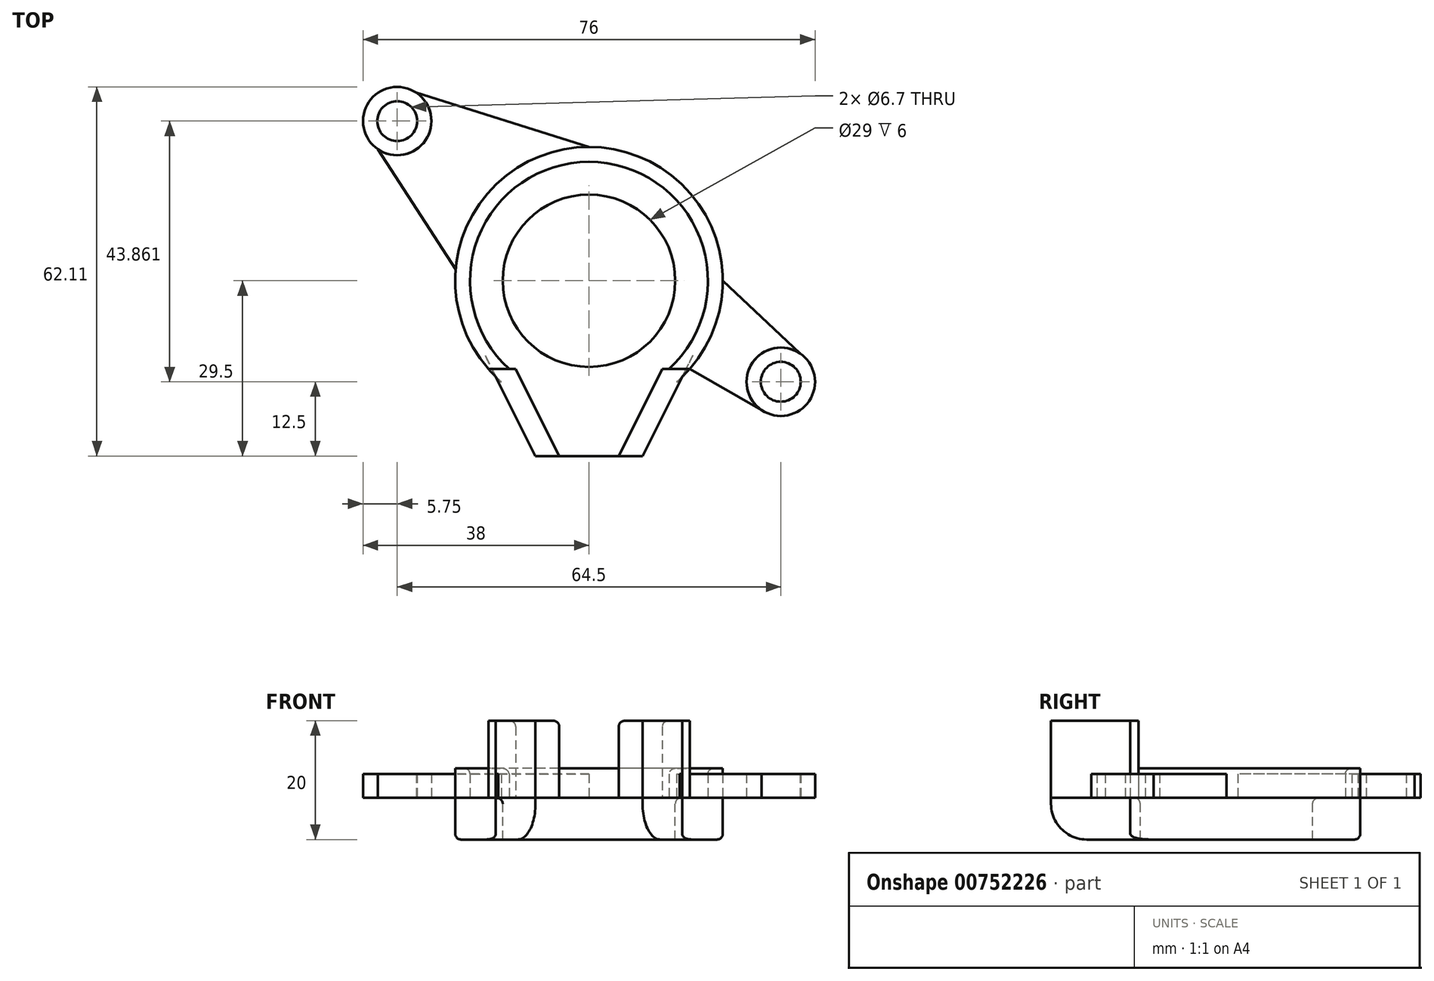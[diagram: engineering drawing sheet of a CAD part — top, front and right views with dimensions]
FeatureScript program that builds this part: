
annotation { "Feature Type Name" : "Feature", "Feature Type Description" : "" }
export const myFeature = defineFeature(function(context is Context, id is Id, definition is map)
    precondition{}
    {
        {
            var Q0;
            Q0=qCreatedBy(makeId("Top.planeOp"),FACE);
            var sketch = newSketch(context, id + "F0", { "sketchPlane" : qUnion([Q0])});
            skCircle(sketch, "E0", {"center": v(-32.25, 26.86) * mm, "radius": 5.75 * mm});
            skCircle(sketch, "E1", {"center": v(32.25, -17) * mm, "radius": 5.75 * mm});
            skCircle(sketch, "E2", {"center": v(32.25, -17) * mm, "radius": 3.35 * mm});
            skCircle(sketch, "E3", {"center": v(-32.25, 26.86) * mm, "radius": 3.35 * mm});
            skCircle(sketch, "E4", {"center": v(0, 0) * mm, "radius": 20 * mm});
            skCircle(sketch, "E5", {"center": v(0, 0) * mm, "radius": 14.5 * mm});
            skLineSegment(sketch, "E6", {"start": v(-32.25, -17) * mm, "end": v(32.25, -17) * mm});
            skCircle(sketch, "E7", {"center": v(-32.25, -17) * mm, "radius": 5.75 * mm});
            skCircle(sketch, "E8", {"center": v(-32.25, -17) * mm, "radius": 3.35 * mm});
            skLineSegment(sketch, "E9", {"start": v(-32.25, 26.86) * mm, "end": v(32.25, 26.86) * mm});
            skCircle(sketch, "E10", {"center": v(32.25, 26.86) * mm, "radius": 5.75 * mm});
            skCircle(sketch, "E11", {"center": v(32.25, 26.86) * mm, "radius": 3.35 * mm});
            skLineSegment(sketch, "E12", {"start": v(-5, -29.5) * mm, "end": v(5, -29.5) * mm});
            skLineSegment(sketch, "E13", {"start": v(-5, -29.5) * mm, "end": v(-9, -29.5) * mm});
            skLineSegment(sketch, "E14", {"start": v(5, -29.5) * mm, "end": v(9, -29.5) * mm});
            skLineSegment(sketch, "E15", {"start": v(-5, -29.5) * mm, "end": v(-12.33, -14.82) * mm});
            skLineSegment(sketch, "E16", {"start": v(-12.33, -14.82) * mm, "end": v(12.33, -14.82) * mm});
            skLineSegment(sketch, "E17", {"start": v(12.33, -14.82) * mm, "end": v(5, -29.5) * mm});
            skLineSegment(sketch, "E18", {"start": v(-12.33, -14.82) * mm, "end": v(-16.33, -14.82) * mm});
            skLineSegment(sketch, "E19", {"start": v(-16.33, -14.82) * mm, "end": v(-9, -29.5) * mm});
            skLineSegment(sketch, "E20", {"start": v(9, -29.5) * mm, "end": v(16.32, -14.82) * mm});
            skLineSegment(sketch, "E21", {"start": v(16.32, -14.82) * mm, "end": v(12.33, -14.82) * mm});
            skCircle(sketch, "E22", {"center": v(0, 0) * mm, "radius": 22.5 * mm});
            skLineSegment(sketch, "E23", {"start": v(-32.25, -17) * mm, "end": v(-32.25, 0) * mm});
            skLineSegment(sketch, "E24", {"start": v(-32.25, 0) * mm, "end": v(-32.25, 26.86) * mm});
            skLineSegment(sketch, "E25", {"start": v(-32.25, 26.86) * mm, "end": v(32.25, -17) * mm});
            skPoint(sketch, "E26.trimOffspring.end.orphan", {"position": v(0, -29.5) * mm});
            skLineSegment(sketch, "E27", {"start": v(0, -29.5) * mm, "end": v(0, 26.86) * mm});
            skLineSegment(sketch, "E28", {"start": v(32.25, 26.86) * mm, "end": v(32.25, 0) * mm});
            skLineSegment(sketch, "E29", {"start": v(32.25, 0) * mm, "end": v(32.25, -17) * mm});
            skLineSegment(sketch, "E30", {"start": v(-16.33, -14.82) * mm, "end": v(-16.93, -14.82) * mm});
            skLineSegment(sketch, "E31", {"start": v(16.32, -14.82) * mm, "end": v(16.93, -14.82) * mm});
            skLineSegment(sketch, "E32", {"start": v(-32.25, 26.86) * mm, "end": v(-29.02, 31.62) * mm});
            skLineSegment(sketch, "E33", {"start": v(-32.25, 26.86) * mm, "end": v(-35.48, 22.1) * mm});
            skLineSegment(sketch, "E34", {"start": v(-35.48, 22.1) * mm, "end": v(-22.42, 1.9) * mm});
            skLineSegment(sketch, "E35", {"start": v(-29.02, 31.62) * mm, "end": v(0, 22.5) * mm});
            skLineSegment(sketch, "E36", {"start": v(32.25, -17) * mm, "end": v(35.48, -12.25) * mm});
            skLineSegment(sketch, "E37", {"start": v(32.25, -17) * mm, "end": v(29.02, -21.75) * mm});
            skLineSegment(sketch, "E38", {"start": v(35.48, -12.25) * mm, "end": v(22.5, 0) * mm});
            skLineSegment(sketch, "E39", {"start": v(29.02, -21.75) * mm, "end": v(16.93, -14.82) * mm});
            skSolve(sketch);
        }
        {
            var Q0;
            {var subQ0=sQuery(id+"F0.wireOp",EDGE,"E32");var subQ5=sQuery(id+"F0.wireOp",EDGE,"E3");var subQ6=makeQuery(id+"F0.imprint","INTERSECT",VERTEX,{"derivedFrom":[subQ5,subQ0]});Q0=makeQuery(id+"F0.imprint","IMPRINT",FACE,{"disambiguationData":[TD([[makeQuery(id+"F0.imprint","IMPRINT",EDGE,{"disambiguationData":[TD([[subQ6,-1.0]])],"derivedFrom":subQ5}),-1.0]])]});}
            var Q1;
            {var subQ0=sQuery(id+"F0.wireOp",EDGE,"E32");var subQ5=sQuery(id+"F0.wireOp",EDGE,"E3");var subQ6=makeQuery(id+"F0.imprint","INTERSECT",VERTEX,{"derivedFrom":[subQ5,subQ0]});Q1=makeQuery(id+"F0.imprint","IMPRINT",FACE,{"disambiguationData":[TD([[makeQuery(id+"F0.imprint","IMPRINT",EDGE,{"disambiguationData":[TD([[subQ6,1.0]])],"derivedFrom":subQ5}),-1.0]])]});}
            var Q2;
            {var subQ0=sQuery(id+"F0.wireOp",EDGE,"E9");var subQ1=sQuery(id+"F0.wireOp",EDGE,"E0");var subQ2=makeQuery(id+"F0.imprint","INTERSECT",VERTEX,{"derivedFrom":[subQ1,subQ0]});Q2=makeQuery(id+"F0.imprint","IMPRINT",FACE,{"disambiguationData":[TD([[makeQuery(id+"F0.imprint","IMPRINT",EDGE,{"disambiguationData":[TD([[subQ2,1.0]])],"derivedFrom":subQ1}),1.0]])]});}
            var Q3;
            {var subQ0=sQuery(id+"F0.wireOp",EDGE,"E24");var subQ1=sQuery(id+"F0.wireOp",EDGE,"E0");var subQ2=makeQuery(id+"F0.imprint","INTERSECT",VERTEX,{"derivedFrom":[subQ1,subQ0]});Q3=makeQuery(id+"F0.imprint","IMPRINT",FACE,{"disambiguationData":[TD([[makeQuery(id+"F0.imprint","IMPRINT",EDGE,{"disambiguationData":[TD([[subQ2,-1.0]])],"derivedFrom":subQ1}),1.0]])]});}
            var Q4;
            {var subQ0=sQuery(id+"F0.wireOp",EDGE,"E33");var subQ5=sQuery(id+"F0.wireOp",EDGE,"E3");var subQ6=makeQuery(id+"F0.imprint","INTERSECT",VERTEX,{"derivedFrom":[subQ5,subQ0]});Q4=makeQuery(id+"F0.imprint","IMPRINT",FACE,{"disambiguationData":[TD([[makeQuery(id+"F0.imprint","IMPRINT",EDGE,{"disambiguationData":[TD([[subQ6,-1.0]])],"derivedFrom":subQ5}),-1.0]])]});}
            var Q5;
            {var subQ0=sQuery(id+"F0.wireOp",EDGE,"E29");var subQ1=sQuery(id+"F0.wireOp",EDGE,"E1");var subQ2=makeQuery(id+"F0.imprint","INTERSECT",VERTEX,{"derivedFrom":[subQ1,subQ0]});Q5=makeQuery(id+"F0.imprint","IMPRINT",FACE,{"disambiguationData":[TD([[makeQuery(id+"F0.imprint","IMPRINT",EDGE,{"disambiguationData":[TD([[subQ2,-1.0]])],"derivedFrom":subQ1}),1.0]])]});}
            var Q6;
            {var subQ3=sQuery(id+"F0.wireOp",EDGE,"E29");var subQ5=sQuery(id+"F0.wireOp",EDGE,"E2");var subQ6=makeQuery(id+"F0.imprint","INTERSECT",VERTEX,{"derivedFrom":[subQ5,subQ3]});Q6=makeQuery(id+"F0.imprint","IMPRINT",FACE,{"disambiguationData":[TD([[makeQuery(id+"F0.imprint","IMPRINT",EDGE,{"disambiguationData":[TD([[subQ6,1.0]])],"derivedFrom":subQ5}),-1.0]])]});}
            var Q7;
            {var subQ0=sQuery(id+"F0.wireOp",EDGE,"E36");var subQ5=sQuery(id+"F0.wireOp",EDGE,"E2");var subQ6=makeQuery(id+"F0.imprint","INTERSECT",VERTEX,{"derivedFrom":[subQ5,subQ0]});Q7=makeQuery(id+"F0.imprint","IMPRINT",FACE,{"disambiguationData":[TD([[makeQuery(id+"F0.imprint","IMPRINT",EDGE,{"disambiguationData":[TD([[subQ6,1.0]])],"derivedFrom":subQ5}),-1.0]])]});}
            var Q8;
            {var subQ0=sQuery(id+"F0.wireOp",EDGE,"E25");var subQ1=sQuery(id+"F0.wireOp",EDGE,"E1");var subQ2=makeQuery(id+"F0.imprint","INTERSECT",VERTEX,{"derivedFrom":[subQ1,subQ0]});Q8=makeQuery(id+"F0.imprint","IMPRINT",FACE,{"disambiguationData":[TD([[makeQuery(id+"F0.imprint","IMPRINT",EDGE,{"disambiguationData":[TD([[subQ2,-1.0]])],"derivedFrom":subQ1}),1.0]])]});}
            var Q9;
            {var subQ3=sQuery(id+"F0.wireOp",EDGE,"E6");var subQ5=sQuery(id+"F0.wireOp",EDGE,"E2");var subQ6=makeQuery(id+"F0.imprint","INTERSECT",VERTEX,{"derivedFrom":[subQ5,subQ3]});Q9=makeQuery(id+"F0.imprint","IMPRINT",FACE,{"disambiguationData":[TD([[makeQuery(id+"F0.imprint","IMPRINT",EDGE,{"disambiguationData":[TD([[subQ6,-1.0]])],"derivedFrom":subQ5}),-1.0]])]});}
            extrude(context, id + "F1", {"entities" : qUnion([Q0, Q1, Q2, Q3, Q4, Q5, Q6, Q7, Q8, Q9]), "depth" : 4 * mm, "offsetDistance" : 25 * mm});
        }
        {
            var Q0;
            {var subQ5=sQuery(id+"F0.wireOp",EDGE,"Wz8c8u1L-tIaJ-pxJv-zDBa-IqU4CHtZDm8W");var subQ6=sQuery(id+"F0.wireOp",EDGE,"E0");var subQ7=makeQuery(id+"F0.imprint","INTERSECT",VERTEX,{"derivedFrom":[subQ6,subQ5]});Q0=makeQuery(id+"F0.imprint","IMPRINT",FACE,{"disambiguationData":[TD([[makeQuery(id+"F0.imprint","IMPRINT",EDGE,{"disambiguationData":[TD([[subQ7,-1.0]])],"derivedFrom":subQ6}),-1.0]])]});}
            var Q1;
            {var subQ5=sQuery(id+"F0.wireOp",EDGE,"E0");var subQ10=sQuery(id+"F0.wireOp",EDGE,"E9");var subQ11=makeQuery(id+"F0.imprint","INTERSECT",VERTEX,{"derivedFrom":[subQ5,subQ10]});Q1=makeQuery(id+"F0.imprint","IMPRINT",FACE,{"disambiguationData":[TD([[makeQuery(id+"F0.imprint","IMPRINT",EDGE,{"disambiguationData":[TD([[subQ11,1.0]])],"derivedFrom":subQ5}),-1.0]])]});}
            var Q2;
            {var subQ1=sQuery(id+"F0.wireOp",EDGE,"E6");var subQ5=sQuery(id+"F0.wireOp",EDGE,"E1");var subQ6=makeQuery(id+"F0.imprint","INTERSECT",VERTEX,{"derivedFrom":[subQ5,subQ1]});Q2=makeQuery(id+"F0.imprint","IMPRINT",FACE,{"disambiguationData":[TD([[makeQuery(id+"F0.imprint","IMPRINT",EDGE,{"disambiguationData":[TD([[subQ6,1.0]])],"derivedFrom":subQ5}),-1.0]])]});}
            var Q3;
            {var subQ0=sQuery(id+"F0.wireOp",EDGE,"E19");var subQ1=sQuery(id+"F0.wireOp",EDGE,"E6");var subQ2=makeQuery(id+"F0.imprint","INTERSECT",VERTEX,{"derivedFrom":[subQ1,subQ0]});Q3=makeQuery(id+"F0.imprint","IMPRINT",FACE,{"disambiguationData":[TD([[makeQuery(id+"F0.imprint","IMPRINT",EDGE,{"disambiguationData":[TD([[subQ2,-1.0]])],"derivedFrom":subQ1}),1.0]])]});}
            var Q4;
            {var subQ9=sQuery(id+"F0.wireOp",EDGE,"E24");var subQ10=sQuery(id+"F0.wireOp",EDGE,"E0");var subQ11=makeQuery(id+"F0.imprint","INTERSECT",VERTEX,{"derivedFrom":[subQ10,subQ9]});Q4=makeQuery(id+"F0.imprint","IMPRINT",FACE,{"disambiguationData":[TD([[makeQuery(id+"F0.imprint","IMPRINT",EDGE,{"disambiguationData":[TD([[subQ11,-1.0]])],"derivedFrom":subQ10}),-1.0]])]});}
            var Q5;
            {var subQ5=sQuery(id+"F0.wireOp",EDGE,"E29");var subQ6=sQuery(id+"F0.wireOp",EDGE,"E1");var subQ7=makeQuery(id+"F0.imprint","INTERSECT",VERTEX,{"derivedFrom":[subQ6,subQ5]});Q5=makeQuery(id+"F0.imprint","IMPRINT",FACE,{"disambiguationData":[TD([[makeQuery(id+"F0.imprint","IMPRINT",EDGE,{"disambiguationData":[TD([[subQ7,-1.0]])],"derivedFrom":subQ6}),-1.0]])]});}
            var Q6;
            {var subQ0=sQuery(id+"F0.wireOp",EDGE,"E20");var subQ1=sQuery(id+"F0.wireOp",EDGE,"E6");var subQ2=makeQuery(id+"F0.imprint","INTERSECT",VERTEX,{"derivedFrom":[subQ1,subQ0]});Q6=makeQuery(id+"F0.imprint","IMPRINT",FACE,{"disambiguationData":[TD([[makeQuery(id+"F0.imprint","IMPRINT",EDGE,{"disambiguationData":[TD([[subQ2,1.0]])],"derivedFrom":subQ1}),1.0]])]});}
            var Q7;
            {var subQ0=sQuery(id+"F0.wireOp",EDGE,"E34");var subQ3=sQuery(id+"F0.wireOp",EDGE,"E24");var subQ5=makeQuery(id+"F0.imprint","INTERSECT",VERTEX,{"derivedFrom":[subQ3,subQ0]});Q7=makeQuery(id+"F0.imprint","IMPRINT",FACE,{"disambiguationData":[TD([[makeQuery(id+"F0.imprint","IMPRINT",EDGE,{"disambiguationData":[TD([[subQ5,-1.0]])],"derivedFrom":subQ3}),1.0]])]});}
            var Q8;
            {var subQ0=sQuery(id+"F0.wireOp",EDGE,"E39");var subQ3=sQuery(id+"F0.wireOp",EDGE,"E6");var subQ5=makeQuery(id+"F0.imprint","INTERSECT",VERTEX,{"derivedFrom":[subQ3,subQ0]});Q8=makeQuery(id+"F0.imprint","IMPRINT",FACE,{"disambiguationData":[TD([[makeQuery(id+"F0.imprint","IMPRINT",EDGE,{"disambiguationData":[TD([[subQ5,-1.0]])],"derivedFrom":subQ3}),-1.0]])]});}
            var Q9;
            {var subQ0=sQuery(id+"F0.wireOp",EDGE,"E38");var subQ3=sQuery(id+"F0.wireOp",EDGE,"E29");var subQ5=makeQuery(id+"F0.imprint","INTERSECT",VERTEX,{"derivedFrom":[subQ3,subQ0]});Q9=makeQuery(id+"F0.imprint","IMPRINT",FACE,{"disambiguationData":[TD([[makeQuery(id+"F0.imprint","IMPRINT",EDGE,{"disambiguationData":[TD([[subQ5,-1.0]])],"derivedFrom":subQ3}),1.0]])]});}
            extrude(context, id + "F2", {"entities" : qUnion([Q0, Q1, Q2, Q3, Q4, Q5, Q6, Q7, Q8, Q9]), "depth" : 4 * mm, "offsetDistance" : 25 * mm});
        }
        {
            var Q0;
            {var subQ5=sQuery(id+"F0.wireOp",EDGE,"E30");Q0=makeQuery(id+"F0.imprint","IMPRINT",FACE,{"disambiguationData":[TD([[makeQuery(id+"F0.imprint","IMPRINT",EDGE,{"derivedFrom":subQ5}),-1.0]])]});}
            var Q1;
            {var subQ3=sQuery(id+"F0.wireOp",EDGE,"E4");var subQ7=sQuery(id+"F0.wireOp",EDGE,"E25");var subQ9=makeQuery(id+"F0.imprint","INTERSECT",VERTEX,{"disambiguationData":[OD(0.0)],"derivedFrom":[subQ3,subQ7]});Q1=makeQuery(id+"F0.imprint","IMPRINT",FACE,{"disambiguationData":[TD([[makeQuery(id+"F0.imprint","IMPRINT",EDGE,{"disambiguationData":[TD([[subQ9,-1.0]])],"derivedFrom":subQ3}),1.0]])]});}
            var Q2;
            {var subQ0=sQuery(id+"F0.wireOp",EDGE,"E25");var subQ1=sQuery(id+"F0.wireOp",EDGE,"E4");var subQ2=makeQuery(id+"F0.imprint","INTERSECT",VERTEX,{"disambiguationData":[OD(0.0)],"derivedFrom":[subQ1,subQ0]});Q2=makeQuery(id+"F0.imprint","IMPRINT",FACE,{"disambiguationData":[TD([[makeQuery(id+"F0.imprint","IMPRINT",EDGE,{"disambiguationData":[TD([[subQ2,1.0]])],"derivedFrom":subQ1}),-1.0]])]});}
            var Q3;
            {var subQ0=sQuery(id+"F0.wireOp",EDGE,"E27");var subQ1=sQuery(id+"F0.wireOp",EDGE,"E4");var subQ2=makeQuery(id+"F0.imprint","INTERSECT",VERTEX,{"disambiguationData":[OD(0.0)],"derivedFrom":[subQ1,subQ0]});Q3=makeQuery(id+"F0.imprint","IMPRINT",FACE,{"disambiguationData":[TD([[makeQuery(id+"F0.imprint","IMPRINT",EDGE,{"disambiguationData":[TD([[subQ2,1.0]])],"derivedFrom":subQ1}),-1.0]])]});}
            var Q4;
            {var subQ0=sQuery(id+"F0.wireOp",EDGE,"E27");var subQ1=sQuery(id+"F0.wireOp",EDGE,"E4");var subQ2=makeQuery(id+"F0.imprint","INTERSECT",VERTEX,{"disambiguationData":[OD(0.0)],"derivedFrom":[subQ1,subQ0]});Q4=makeQuery(id+"F0.imprint","IMPRINT",FACE,{"disambiguationData":[TD([[makeQuery(id+"F0.imprint","IMPRINT",EDGE,{"disambiguationData":[TD([[subQ2,1.0]])],"derivedFrom":subQ1}),1.0]])]});}
            var Q5;
            {var subQ0=sQuery(id+"F0.wireOp",EDGE,"E25");var subQ1=sQuery(id+"F0.wireOp",EDGE,"E4");var subQ2=makeQuery(id+"F0.imprint","INTERSECT",VERTEX,{"disambiguationData":[OD(0.0)],"derivedFrom":[subQ1,subQ0]});Q5=makeQuery(id+"F0.imprint","IMPRINT",FACE,{"disambiguationData":[TD([[makeQuery(id+"F0.imprint","IMPRINT",EDGE,{"disambiguationData":[TD([[subQ2,1.0]])],"derivedFrom":subQ1}),1.0]])]});}
            var Q6;
            {var subQ0=sQuery(id+"F0.wireOp",EDGE,"E21");var subQ5=sQuery(id+"F0.wireOp",EDGE,"E4");var subQ6=makeQuery(id+"F0.imprint","INTERSECT",VERTEX,{"derivedFrom":[subQ5,subQ0]});Q6=makeQuery(id+"F0.imprint","IMPRINT",FACE,{"disambiguationData":[TD([[makeQuery(id+"F0.imprint","IMPRINT",EDGE,{"disambiguationData":[TD([[subQ6,-1.0]])],"derivedFrom":subQ5}),1.0]])]});}
            var Q7;
            {var subQ7=sQuery(id+"F0.wireOp",EDGE,"E31");Q7=makeQuery(id+"F0.imprint","IMPRINT",FACE,{"disambiguationData":[TD([[makeQuery(id+"F0.imprint","IMPRINT",EDGE,{"derivedFrom":subQ7}),1.0]])]});}
            var Q8;
            {var subQ1=sQuery(id+"F0.wireOp",EDGE,"E15");var subQ3=sQuery(id+"F0.wireOp",EDGE,"E4");var subQ4=makeQuery(id+"F0.imprint","INTERSECT",VERTEX,{"derivedFrom":[subQ3,subQ1]});Q8=makeQuery(id+"F0.imprint","IMPRINT",FACE,{"disambiguationData":[TD([[makeQuery(id+"F0.imprint","IMPRINT",EDGE,{"disambiguationData":[TD([[subQ4,-1.0]])],"derivedFrom":subQ3}),1.0]])]});}
            var Q9;
            {var subQ5=sQuery(id+"F0.wireOp",EDGE,"E6");var subQ6=sQuery(id+"F0.wireOp",EDGE,"E4");var subQ7=makeQuery(id+"F0.imprint","INTERSECT",VERTEX,{"disambiguationData":[OD(1.0)],"derivedFrom":[subQ6,subQ5]});Q9=makeQuery(id+"F0.imprint","IMPRINT",FACE,{"disambiguationData":[TD([[makeQuery(id+"F0.imprint","IMPRINT",EDGE,{"disambiguationData":[TD([[subQ7,-1.0]])],"derivedFrom":subQ6}),1.0]])]});}
            var Q10;
            {var subQ1=sQuery(id+"F0.wireOp",EDGE,"E18");var subQ3=sQuery(id+"F0.wireOp",EDGE,"E4");var subQ4=makeQuery(id+"F0.imprint","INTERSECT",VERTEX,{"derivedFrom":[subQ3,subQ1]});Q10=makeQuery(id+"F0.imprint","IMPRINT",FACE,{"disambiguationData":[TD([[makeQuery(id+"F0.imprint","IMPRINT",EDGE,{"disambiguationData":[TD([[subQ4,-1.0]])],"derivedFrom":subQ3}),-1.0]])]});}
            var Q11;
            {var subQ0=sQuery(id+"F0.wireOp",EDGE,"E18");var subQ1=sQuery(id+"F0.wireOp",EDGE,"E4");var subQ2=makeQuery(id+"F0.imprint","INTERSECT",VERTEX,{"derivedFrom":[subQ1,subQ0]});Q11=makeQuery(id+"F0.imprint","IMPRINT",FACE,{"disambiguationData":[TD([[makeQuery(id+"F0.imprint","IMPRINT",EDGE,{"disambiguationData":[TD([[subQ2,-1.0]])],"derivedFrom":subQ1}),1.0]])]});}
            var Q12;
            {var subQ0=sQuery(id+"F0.wireOp",EDGE,"E30");Q12=makeQuery(id+"F0.imprint","IMPRINT",FACE,{"disambiguationData":[TD([[makeQuery(id+"F0.imprint","IMPRINT",EDGE,{"derivedFrom":subQ0}),1.0]])]});}
            var Q13;
            {var subQ0=sQuery(id+"F0.wireOp",EDGE,"E15");var subQ1=sQuery(id+"F0.wireOp",EDGE,"E4");var subQ2=makeQuery(id+"F0.imprint","INTERSECT",VERTEX,{"derivedFrom":[subQ1,subQ0]});Q13=makeQuery(id+"F0.imprint","IMPRINT",FACE,{"disambiguationData":[TD([[makeQuery(id+"F0.imprint","IMPRINT",EDGE,{"disambiguationData":[TD([[subQ2,-1.0]])],"derivedFrom":subQ1}),-1.0]])]});}
            var Q14;
            {var subQ5=sQuery(id+"F0.wireOp",EDGE,"E6");var subQ6=sQuery(id+"F0.wireOp",EDGE,"E4");var subQ7=makeQuery(id+"F0.imprint","INTERSECT",VERTEX,{"disambiguationData":[OD(0.0)],"derivedFrom":[subQ6,subQ5]});Q14=makeQuery(id+"F0.imprint","IMPRINT",FACE,{"disambiguationData":[TD([[makeQuery(id+"F0.imprint","IMPRINT",EDGE,{"disambiguationData":[TD([[subQ7,-1.0]])],"derivedFrom":subQ6}),-1.0]])]});}
            var Q15;
            {var subQ0=sQuery(id+"F0.wireOp",EDGE,"E6");var subQ1=sQuery(id+"F0.wireOp",EDGE,"E4");var subQ2=makeQuery(id+"F0.imprint","INTERSECT",VERTEX,{"disambiguationData":[OD(0.0)],"derivedFrom":[subQ1,subQ0]});Q15=makeQuery(id+"F0.imprint","IMPRINT",FACE,{"disambiguationData":[TD([[makeQuery(id+"F0.imprint","IMPRINT",EDGE,{"disambiguationData":[TD([[subQ2,-1.0]])],"derivedFrom":subQ1}),1.0]])]});}
            var Q16;
            {var subQ0=sQuery(id+"F0.wireOp",EDGE,"E22");var subQ1=sQuery(id+"F0.wireOp",EDGE,"E6");var subQ2=makeQuery(id+"F0.imprint","INTERSECT",VERTEX,{"disambiguationData":[OD(0.0)],"derivedFrom":[subQ1,subQ0]});Q16=makeQuery(id+"F0.imprint","IMPRINT",FACE,{"disambiguationData":[TD([[makeQuery(id+"F0.imprint","IMPRINT",EDGE,{"disambiguationData":[TD([[subQ2,-1.0]])],"derivedFrom":subQ1}),-1.0]])]});}
            var Q17;
            {var subQ1=sQuery(id+"F0.wireOp",EDGE,"E13");Q17=makeQuery(id+"F0.imprint","IMPRINT",FACE,{"disambiguationData":[TD([[makeQuery(id+"F0.imprint","IMPRINT",EDGE,{"derivedFrom":subQ1}),-1.0]])]});}
            var Q18;
            {var subQ0=sQuery(id+"F0.wireOp",EDGE,"E15");var subQ5=sQuery(id+"F0.wireOp",EDGE,"E22");var subQ6=makeQuery(id+"F0.imprint","INTERSECT",VERTEX,{"derivedFrom":[subQ0,subQ5]});Q18=makeQuery(id+"F0.imprint","IMPRINT",FACE,{"disambiguationData":[TD([[makeQuery(id+"F0.imprint","IMPRINT",EDGE,{"disambiguationData":[TD([[subQ6,-1.0]])],"derivedFrom":subQ5}),-1.0]])]});}
            var Q19;
            {var subQ3=sQuery(id+"F0.wireOp",EDGE,"E27");var subQ7=sQuery(id+"F0.wireOp",EDGE,"E4");var subQ9=makeQuery(id+"F0.imprint","INTERSECT",VERTEX,{"disambiguationData":[OD(1.0)],"derivedFrom":[subQ7,subQ3]});Q19=makeQuery(id+"F0.imprint","IMPRINT",FACE,{"disambiguationData":[TD([[makeQuery(id+"F0.imprint","IMPRINT",EDGE,{"disambiguationData":[TD([[subQ9,-1.0]])],"derivedFrom":subQ7}),-1.0]])]});}
            var Q20;
            {var subQ0=sQuery(id+"F0.wireOp",EDGE,"E27");var subQ1=sQuery(id+"F0.wireOp",EDGE,"E4");var subQ2=makeQuery(id+"F0.imprint","INTERSECT",VERTEX,{"disambiguationData":[OD(1.0)],"derivedFrom":[subQ1,subQ0]});Q20=makeQuery(id+"F0.imprint","IMPRINT",FACE,{"disambiguationData":[TD([[makeQuery(id+"F0.imprint","IMPRINT",EDGE,{"disambiguationData":[TD([[subQ2,-1.0]])],"derivedFrom":subQ1}),1.0]])]});}
            var Q21;
            {var subQ0=sQuery(id+"F0.wireOp",EDGE,"E17");var subQ5=sQuery(id+"F0.wireOp",EDGE,"E22");var subQ7=makeQuery(id+"F0.imprint","INTERSECT",VERTEX,{"derivedFrom":[subQ0,subQ5]});Q21=makeQuery(id+"F0.imprint","IMPRINT",FACE,{"disambiguationData":[TD([[makeQuery(id+"F0.imprint","IMPRINT",EDGE,{"disambiguationData":[TD([[subQ7,1.0]])],"derivedFrom":subQ5}),-1.0]])]});}
            var Q22;
            {var subQ1=sQuery(id+"F0.wireOp",EDGE,"E14");Q22=makeQuery(id+"F0.imprint","IMPRINT",FACE,{"disambiguationData":[TD([[makeQuery(id+"F0.imprint","IMPRINT",EDGE,{"derivedFrom":subQ1}),1.0]])]});}
            var Q23;
            {var subQ0=sQuery(id+"F0.wireOp",EDGE,"E17");var subQ1=sQuery(id+"F0.wireOp",EDGE,"E6");var subQ2=makeQuery(id+"F0.imprint","INTERSECT",VERTEX,{"derivedFrom":[subQ1,subQ0]});Q23=makeQuery(id+"F0.imprint","IMPRINT",FACE,{"disambiguationData":[TD([[makeQuery(id+"F0.imprint","IMPRINT",EDGE,{"disambiguationData":[TD([[subQ2,-1.0]])],"derivedFrom":subQ1}),-1.0]])]});}
            var Q24;
            {var subQ0=sQuery(id+"F0.wireOp",EDGE,"E6");var subQ1=sQuery(id+"F0.wireOp",EDGE,"E4");var subQ2=makeQuery(id+"F0.imprint","INTERSECT",VERTEX,{"disambiguationData":[OD(1.0)],"derivedFrom":[subQ1,subQ0]});Q24=makeQuery(id+"F0.imprint","IMPRINT",FACE,{"disambiguationData":[TD([[makeQuery(id+"F0.imprint","IMPRINT",EDGE,{"disambiguationData":[TD([[subQ2,-1.0]])],"derivedFrom":subQ1}),-1.0]])]});}
            var Q25;
            {var subQ0=sQuery(id+"F0.wireOp",EDGE,"E17");var subQ9=sQuery(id+"F0.wireOp",EDGE,"E4");var subQ10=makeQuery(id+"F0.imprint","INTERSECT",VERTEX,{"derivedFrom":[subQ9,subQ0]});Q25=makeQuery(id+"F0.imprint","IMPRINT",FACE,{"disambiguationData":[TD([[makeQuery(id+"F0.imprint","IMPRINT",EDGE,{"disambiguationData":[TD([[subQ10,-1.0]])],"derivedFrom":subQ9}),-1.0]])]});}
            var Q26;
            {var subQ0=sQuery(id+"F0.wireOp",EDGE,"E17");var subQ1=sQuery(id+"F0.wireOp",EDGE,"E4");var subQ2=makeQuery(id+"F0.imprint","INTERSECT",VERTEX,{"derivedFrom":[subQ1,subQ0]});Q26=makeQuery(id+"F0.imprint","IMPRINT",FACE,{"disambiguationData":[TD([[makeQuery(id+"F0.imprint","IMPRINT",EDGE,{"disambiguationData":[TD([[subQ2,-1.0]])],"derivedFrom":subQ1}),1.0]])]});}
            var Q27;
            {var subQ0=sQuery(id+"F0.wireOp",EDGE,"E20");var subQ1=sQuery(id+"F0.wireOp",EDGE,"E6");var subQ2=makeQuery(id+"F0.imprint","INTERSECT",VERTEX,{"derivedFrom":[subQ1,subQ0]});Q27=makeQuery(id+"F0.imprint","IMPRINT",FACE,{"disambiguationData":[TD([[makeQuery(id+"F0.imprint","IMPRINT",EDGE,{"disambiguationData":[TD([[subQ2,1.0]])],"derivedFrom":subQ1}),1.0]])]});}
            var Q28;
            {var subQ0=sQuery(id+"F0.wireOp",EDGE,"E31");Q28=makeQuery(id+"F0.imprint","IMPRINT",FACE,{"disambiguationData":[TD([[makeQuery(id+"F0.imprint","IMPRINT",EDGE,{"derivedFrom":subQ0}),-1.0]])]});}
            var Q29;
            {var subQ0=sQuery(id+"F0.wireOp",EDGE,"E19");var subQ1=sQuery(id+"F0.wireOp",EDGE,"E6");var subQ2=makeQuery(id+"F0.imprint","INTERSECT",VERTEX,{"derivedFrom":[subQ1,subQ0]});Q29=makeQuery(id+"F0.imprint","IMPRINT",FACE,{"disambiguationData":[TD([[makeQuery(id+"F0.imprint","IMPRINT",EDGE,{"disambiguationData":[TD([[subQ2,-1.0]])],"derivedFrom":subQ1}),1.0]])]});}
            extrude(context, id + "F3", {"entities" : qUnion([Q0, Q1, Q2, Q3, Q4, Q5, Q6, Q7, Q8, Q9, Q10, Q11, Q12, Q13, Q14, Q15, Q16, Q17, Q18, Q19, Q20, Q21, Q22, Q23, Q24, Q25, Q26, Q27, Q28, Q29]), "depth" : -7 * mm, "offsetDistance" : 25 * mm});
        }
        {
            var Q0;
            {var subQ5=sQuery(id+"F0.wireOp",EDGE,"E30");Q0=makeQuery(id+"F0.imprint","IMPRINT",FACE,{"disambiguationData":[TD([[makeQuery(id+"F0.imprint","IMPRINT",EDGE,{"derivedFrom":subQ5}),-1.0]])]});}
            var Q1;
            {var subQ0=sQuery(id+"F0.wireOp",EDGE,"E25");var subQ1=sQuery(id+"F0.wireOp",EDGE,"E4");var subQ2=makeQuery(id+"F0.imprint","INTERSECT",VERTEX,{"disambiguationData":[OD(0.0)],"derivedFrom":[subQ1,subQ0]});Q1=makeQuery(id+"F0.imprint","IMPRINT",FACE,{"disambiguationData":[TD([[makeQuery(id+"F0.imprint","IMPRINT",EDGE,{"disambiguationData":[TD([[subQ2,1.0]])],"derivedFrom":subQ1}),-1.0]])]});}
            var Q2;
            {var subQ0=sQuery(id+"F0.wireOp",EDGE,"E27");var subQ1=sQuery(id+"F0.wireOp",EDGE,"E4");var subQ2=makeQuery(id+"F0.imprint","INTERSECT",VERTEX,{"disambiguationData":[OD(0.0)],"derivedFrom":[subQ1,subQ0]});Q2=makeQuery(id+"F0.imprint","IMPRINT",FACE,{"disambiguationData":[TD([[makeQuery(id+"F0.imprint","IMPRINT",EDGE,{"disambiguationData":[TD([[subQ2,1.0]])],"derivedFrom":subQ1}),-1.0]])]});}
            var Q3;
            {var subQ7=sQuery(id+"F0.wireOp",EDGE,"E31");Q3=makeQuery(id+"F0.imprint","IMPRINT",FACE,{"disambiguationData":[TD([[makeQuery(id+"F0.imprint","IMPRINT",EDGE,{"derivedFrom":subQ7}),1.0]])]});}
            extrude(context, id + "F4", {"entities" : qUnion([Q0, Q1, Q2, Q3]), "depth" : 5 * mm, "offsetDistance" : 25 * mm});
        }
        {
            var Q0;
            {var subQ0=sQuery(id+"F0.wireOp",EDGE,"E18");var subQ1=sQuery(id+"F0.wireOp",EDGE,"E4");var subQ2=makeQuery(id+"F0.imprint","INTERSECT",VERTEX,{"derivedFrom":[subQ1,subQ0]});Q0=makeQuery(id+"F0.imprint","IMPRINT",FACE,{"disambiguationData":[TD([[makeQuery(id+"F0.imprint","IMPRINT",EDGE,{"disambiguationData":[TD([[subQ2,-1.0]])],"derivedFrom":subQ1}),1.0]])]});}
            var Q1;
            {var subQ1=sQuery(id+"F0.wireOp",EDGE,"E18");var subQ3=sQuery(id+"F0.wireOp",EDGE,"E4");var subQ4=makeQuery(id+"F0.imprint","INTERSECT",VERTEX,{"derivedFrom":[subQ3,subQ1]});Q1=makeQuery(id+"F0.imprint","IMPRINT",FACE,{"disambiguationData":[TD([[makeQuery(id+"F0.imprint","IMPRINT",EDGE,{"disambiguationData":[TD([[subQ4,-1.0]])],"derivedFrom":subQ3}),-1.0]])]});}
            var Q2;
            {var subQ0=sQuery(id+"F0.wireOp",EDGE,"E30");Q2=makeQuery(id+"F0.imprint","IMPRINT",FACE,{"disambiguationData":[TD([[makeQuery(id+"F0.imprint","IMPRINT",EDGE,{"derivedFrom":subQ0}),1.0]])]});}
            var Q3;
            {var subQ0=sQuery(id+"F0.wireOp",EDGE,"E19");var subQ1=sQuery(id+"F0.wireOp",EDGE,"E6");var subQ2=makeQuery(id+"F0.imprint","INTERSECT",VERTEX,{"derivedFrom":[subQ1,subQ0]});Q3=makeQuery(id+"F0.imprint","IMPRINT",FACE,{"disambiguationData":[TD([[makeQuery(id+"F0.imprint","IMPRINT",EDGE,{"disambiguationData":[TD([[subQ2,-1.0]])],"derivedFrom":subQ1}),1.0]])]});}
            var Q4;
            {var subQ1=sQuery(id+"F0.wireOp",EDGE,"E13");Q4=makeQuery(id+"F0.imprint","IMPRINT",FACE,{"disambiguationData":[TD([[makeQuery(id+"F0.imprint","IMPRINT",EDGE,{"derivedFrom":subQ1}),-1.0]])]});}
            var Q5;
            {var subQ0=sQuery(id+"F0.wireOp",EDGE,"E22");var subQ1=sQuery(id+"F0.wireOp",EDGE,"E6");var subQ2=makeQuery(id+"F0.imprint","INTERSECT",VERTEX,{"disambiguationData":[OD(0.0)],"derivedFrom":[subQ1,subQ0]});Q5=makeQuery(id+"F0.imprint","IMPRINT",FACE,{"disambiguationData":[TD([[makeQuery(id+"F0.imprint","IMPRINT",EDGE,{"disambiguationData":[TD([[subQ2,-1.0]])],"derivedFrom":subQ1}),-1.0]])]});}
            var Q6;
            {var subQ1=sQuery(id+"F0.wireOp",EDGE,"E14");Q6=makeQuery(id+"F0.imprint","IMPRINT",FACE,{"disambiguationData":[TD([[makeQuery(id+"F0.imprint","IMPRINT",EDGE,{"derivedFrom":subQ1}),1.0]])]});}
            var Q7;
            {var subQ0=sQuery(id+"F0.wireOp",EDGE,"E17");var subQ1=sQuery(id+"F0.wireOp",EDGE,"E6");var subQ2=makeQuery(id+"F0.imprint","INTERSECT",VERTEX,{"derivedFrom":[subQ1,subQ0]});Q7=makeQuery(id+"F0.imprint","IMPRINT",FACE,{"disambiguationData":[TD([[makeQuery(id+"F0.imprint","IMPRINT",EDGE,{"disambiguationData":[TD([[subQ2,-1.0]])],"derivedFrom":subQ1}),-1.0]])]});}
            var Q8;
            {var subQ0=sQuery(id+"F0.wireOp",EDGE,"E17");var subQ9=sQuery(id+"F0.wireOp",EDGE,"E4");var subQ10=makeQuery(id+"F0.imprint","INTERSECT",VERTEX,{"derivedFrom":[subQ9,subQ0]});Q8=makeQuery(id+"F0.imprint","IMPRINT",FACE,{"disambiguationData":[TD([[makeQuery(id+"F0.imprint","IMPRINT",EDGE,{"disambiguationData":[TD([[subQ10,-1.0]])],"derivedFrom":subQ9}),-1.0]])]});}
            var Q9;
            {var subQ0=sQuery(id+"F0.wireOp",EDGE,"E31");Q9=makeQuery(id+"F0.imprint","IMPRINT",FACE,{"disambiguationData":[TD([[makeQuery(id+"F0.imprint","IMPRINT",EDGE,{"derivedFrom":subQ0}),-1.0]])]});}
            var Q10;
            {var subQ0=sQuery(id+"F0.wireOp",EDGE,"E17");var subQ1=sQuery(id+"F0.wireOp",EDGE,"E4");var subQ2=makeQuery(id+"F0.imprint","INTERSECT",VERTEX,{"derivedFrom":[subQ1,subQ0]});Q10=makeQuery(id+"F0.imprint","IMPRINT",FACE,{"disambiguationData":[TD([[makeQuery(id+"F0.imprint","IMPRINT",EDGE,{"disambiguationData":[TD([[subQ2,-1.0]])],"derivedFrom":subQ1}),1.0]])]});}
            var Q11;
            {var subQ0=sQuery(id+"F0.wireOp",EDGE,"E20");var subQ1=sQuery(id+"F0.wireOp",EDGE,"E6");var subQ2=makeQuery(id+"F0.imprint","INTERSECT",VERTEX,{"derivedFrom":[subQ1,subQ0]});Q11=makeQuery(id+"F0.imprint","IMPRINT",FACE,{"disambiguationData":[TD([[makeQuery(id+"F0.imprint","IMPRINT",EDGE,{"disambiguationData":[TD([[subQ2,1.0]])],"derivedFrom":subQ1}),1.0]])]});}
            extrude(context, id + "F5", {"entities" : qUnion([Q0, Q1, Q2, Q3, Q4, Q5, Q6, Q7, Q8, Q9, Q10, Q11]), "depth" : 13 * mm, "offsetDistance" : 25 * mm});
        }
        {
            var Q0;
            Q0=makeQuery(id+"F5.opExtrude","CAP_EDGE",EDGE,{"disambiguationData":[OSD([sQuery(id+"F0.wireOp",EDGE,"E15")])],"isStart":false});
            fillet(context, id + "F6", {"entities" : qUnion([Q0]), "radius" : 1 * mm, "tangentPropagation" : true, "allowEdgeOverflow" : false});
        }
        {
            var Q0;
            Q0=makeQuery(id+"F5.opExtrude","CAP_EDGE",EDGE,{"disambiguationData":[OSD([sQuery(id+"F0.wireOp",EDGE,"E17")])],"isStart":false});
            fillet(context, id + "F7", {"entities" : qUnion([Q0]), "radius" : 1 * mm, "tangentPropagation" : true, "allowEdgeOverflow" : false});
        }
        {
            var Q0;
            Q0=makeQuery(id+"F4.opExtrude","CAP_EDGE",EDGE,{"disambiguationData":[OSD([sQuery(id+"F0.wireOp",EDGE,"E4")])],"isStart":false});
            fillet(context, id + "F8", {"entities" : qUnion([Q0]), "radius" : 1 * mm, "tangentPropagation" : true, "allowEdgeOverflow" : false});
        }
        {
            var Q0;
            Q0=makeQuery(id+"F3.opExtrude","CAP_EDGE",EDGE,{"disambiguationData":[OSD([sQuery(id+"F0.wireOp",EDGE,"E5")])],"isStart":true});
            fillet(context, id + "F9", {"entities" : qUnion([Q0]), "radius" : 1 * mm, "tangentPropagation" : true, "allowEdgeOverflow" : false});
        }
        {
            var Q0;
            Q0=makeQuery(id+"F3.opExtrude","CAP_EDGE",EDGE,{"disambiguationData":[OSD([sQuery(id+"F0.wireOp",EDGE,"E12"),sQuery(id+"F0.wireOp",EDGE,"E13"),sQuery(id+"F0.wireOp",EDGE,"E14")])],"isStart":false});
            fillet(context, id + "F10", {"entities" : qUnion([Q0]), "radius" : 6 * mm, "tangentPropagation" : true, "allowEdgeOverflow" : false});
        }
        {
            var Q0;
            Q0=makeQuery(id+"F3.opExtrude","CAP_EDGE",EDGE,{"disambiguationData":[OSD([sQuery(id+"F0.wireOp",EDGE,"E22")])],"isStart":false});
            fillet(context, id + "F11", {"entities" : qUnion([Q0]), "radius" : 1 * mm, "tangentPropagation" : true, "allowEdgeOverflow" : false});
        }
    });
